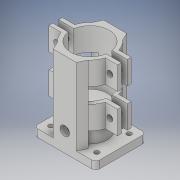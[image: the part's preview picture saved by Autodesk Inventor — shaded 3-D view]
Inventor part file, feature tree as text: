
AUTODESK INVENTOR PART (.ipt)
format: ipt  version: 2018 (Build 220112000, 112)  size: 306,176 bytes
history: native  units: in
note: dims shown in document units (in); Inventor stores cm internally (conversion verified against a paired STEP export)
features: extrude x6, sketch x6, plane x1, mirror x1, fillet x1
ambient origin geometry x8: Origin, YZ Plane, XZ Plane, XY Plane, X Axis, Y Axis, Z Axis, Center Point
bodies: Solid1 (feature_tree)
feature tree (15):
  extrude  "Extrusion1"  Depth=1.64in
  plane  "Work Plane1"
  extrude  "Extrusion3"  Depth=2.01in
  extrude  "Extrusion4"  Depth=0.257in
  extrude  "Extrusion5"  Depth=0.257in
  mirror  "Mirror1"
  extrude  "Extrusion6"  Depth=0.25in
  extrude  "Extrusion7"  Depth=0.125in
  fillet  "Fillet1"  Radius=0.1875in
  sketch  "Sketch1"  dims[d0=0.1562in d1=1.64in]
  sketch  "Sketch3"  dims[d2=2.01in d3=0.24in]
  sketch  "Sketch6"  dims[d4=0.293in d5=0.257in]
  sketch  "Sketch7"  dims[d6=0.293in d7=0.257in]
  sketch  "Sketch8"  dims[d8=0.25in d9=0.0in d10=2.5in]
  sketch  "Sketch9"  dims[d20=0.125in d21=1.25in d22=0.125in d23=0.125in d24=0.1875in d25=0.0938in d26=0.625in d27=0.125in d28=0.125in d29=0.125in d30=0.0938in d31=0.0938in d32=0.75in d33=0.375in d34=1.0in d35=2.5in d36=0.0in d37=0.5in d38=0.5in d39=0.75in d40=2.5in d41=0.0in d43=0.5in d44=0.5in d45=0.25in d46=0.25in d47=0.25in d48=0.25in d49=2.5in d50=0.0in d51=0.1935in d52=1.13in d53=0.75in d54=0.0in d55=0.31in d57=0.381in d58=2.4375in d59=0.0in d60=0.125in]
